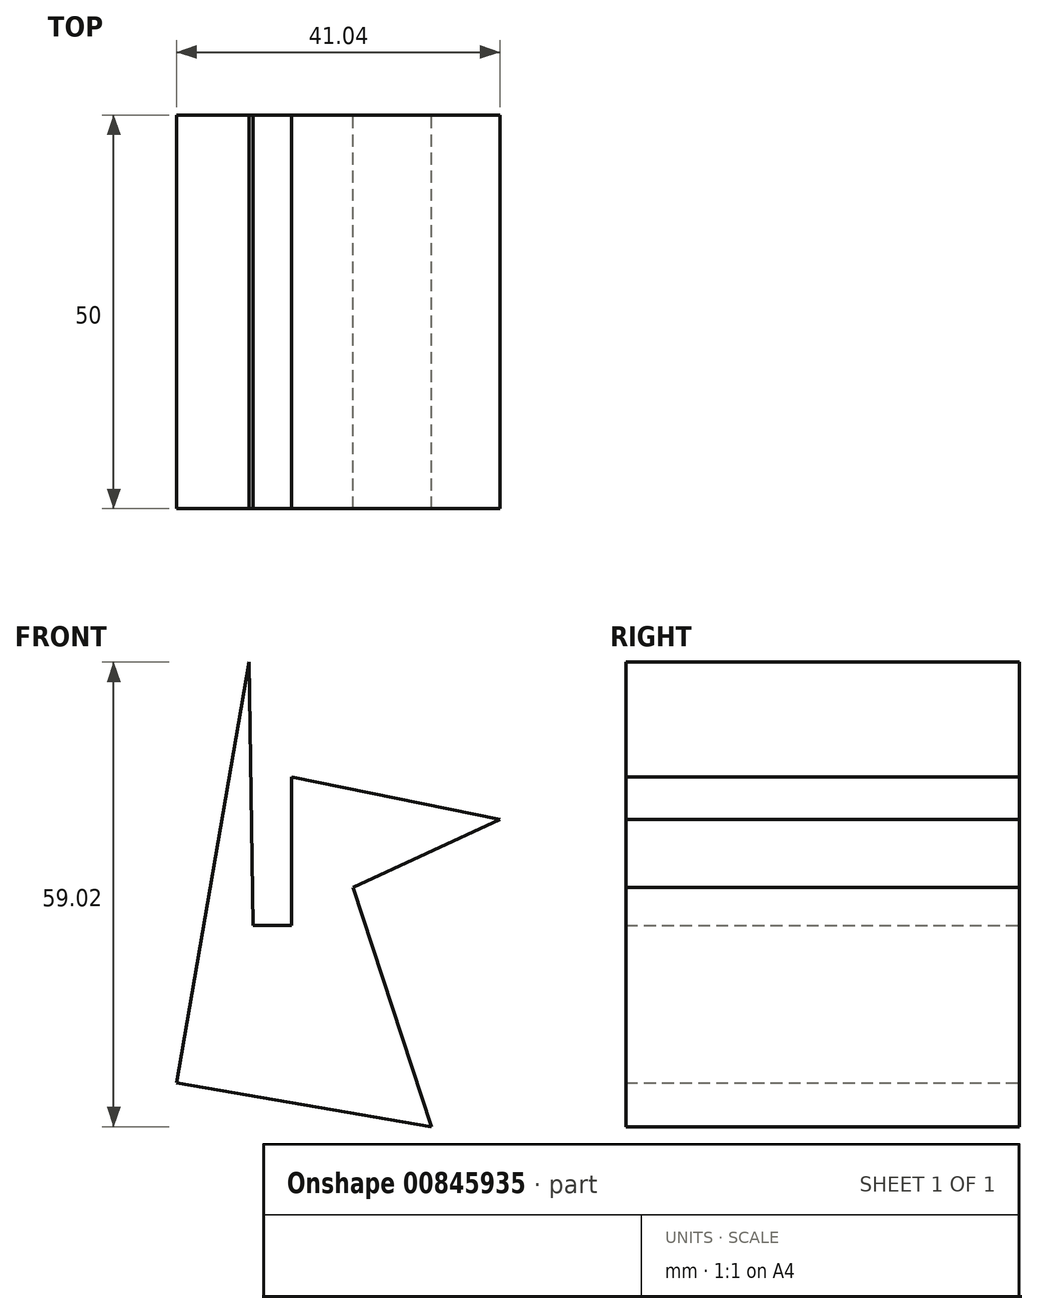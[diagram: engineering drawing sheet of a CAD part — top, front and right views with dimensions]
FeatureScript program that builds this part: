
annotation { "Feature Type Name" : "Feature", "Feature Type Description" : "" }
export const myFeature = defineFeature(function(context is Context, id is Id, definition is map)
    precondition{}
    {
        {
            var Q0;
            Q0=qCreatedBy(makeId("Front.planeOp"),FACE);
            var sketch = newSketch(context, id + "F0", { "sketchPlane" : qUnion([Q0])});
            skLineSegment(sketch, "E0", {"start": v(-41.52, 38.14) * mm, "end": v(-50.7, -15.33) * mm});
            skLineSegment(sketch, "E1", {"start": v(-50.7, -15.33) * mm, "end": v(-18.37, -20.88) * mm});
            skLineSegment(sketch, "E2", {"start": v(-18.37, -20.88) * mm, "end": v(-28.29, 9.52) * mm});
            skLineSegment(sketch, "E3", {"start": v(-28.29, 9.52) * mm, "end": v(-9.66, 18.16) * mm});
            skLineSegment(sketch, "E4", {"start": v(-9.66, 18.16) * mm, "end": v(-36.12, 23.56) * mm});
            skLineSegment(sketch, "E5", {"start": v(-36.12, 23.56) * mm, "end": v(-36.12, 4.66) * mm});
            skLineSegment(sketch, "E6", {"start": v(-36.12, 4.66) * mm, "end": v(-40.98, 4.66) * mm});
            skLineSegment(sketch, "E7", {"start": v(-40.98, 4.66) * mm, "end": v(-41.52, 38.14) * mm});
            skSolve(sketch);
        }
        {
            var Q0;
            Q0=makeQuery(id+"F0.imprint","IMPRINT",FACE,{"disambiguationData":[TD([[makeQuery(id+"F0.imprint","IMPRINT",EDGE,{"derivedFrom":sQuery(id+"F0.wireOp",EDGE,"E0")}),1.0]])]});
            extrude(context, id + "F1", {"entities" : qUnion([Q0]), "depth" : 50 * mm, "offsetDistance" : 25.4 * mm});
        }
    });
